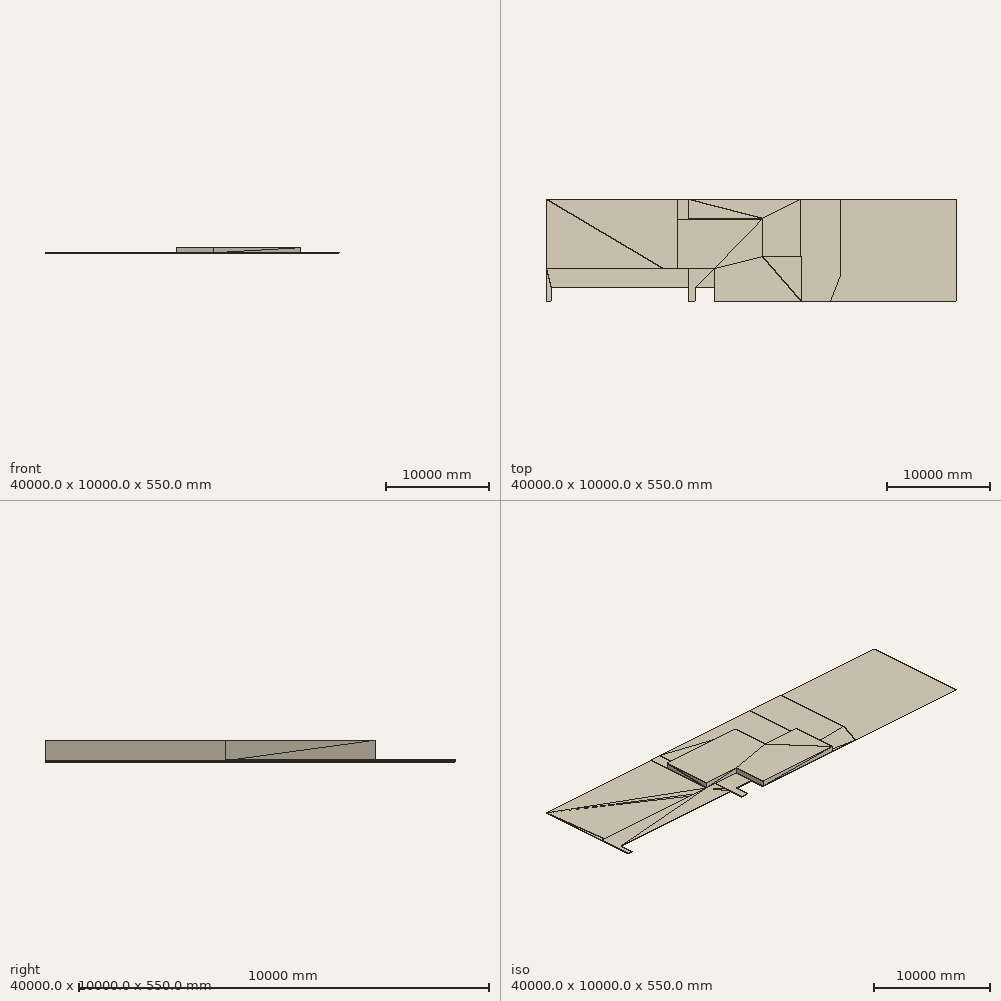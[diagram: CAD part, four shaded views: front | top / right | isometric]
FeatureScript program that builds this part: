
annotation { "Feature Type Name" : "Feature", "Feature Type Description" : "" }
export const myFeature = defineFeature(function(context is Context, id is Id, definition is map)
    precondition{}
    {
        {
            var Q0;
            Q0=qCreatedBy(makeId("Top.planeOp"),FACE);
            var sketch = newSketch(context, id + "F0", { "sketchPlane" : qUnion([Q0])});
            skLineSegment(sketch, "E0.bottom", {"start": v(-20000, -5000) * mm, "end": v(20000, -5000) * mm});
            skLineSegment(sketch, "E0.top", {"start": v(-20000, 5000) * mm, "end": v(20000, 5000) * mm});
            skLineSegment(sketch, "E0.left", {"start": v(-20000, -5000) * mm, "end": v(-20000, 5000) * mm});
            skLineSegment(sketch, "E0.right", {"start": v(20000, -5000) * mm, "end": v(20000, 5000) * mm});
            skPoint(sketch, "E0.middle", {"position": v(0, 0) * mm});
            skSolve(sketch);
        }
        {
            var Q0;
            Q0 = qSketchRegion(id + "F0", true);
            extrude(context, id + "F1", {"entities" : qUnion([Q0]), "depth" : 25 * mm});
        }
        {
            var Q0;
            Q0=makeQuery(id+"F1.opExtrude","CAP_FACE",FACE,{"disambiguationData":[OSD([sQuery(id+"F0.wireOp",EDGE,"E0.bottom"),sQuery(id+"F0.wireOp",EDGE,"E0.top"),sQuery(id+"F0.wireOp",EDGE,"E0.left"),sQuery(id+"F0.wireOp",EDGE,"E0.right")])],"isStart":false});
            var sketch = newSketch(context, id + "F2", { "sketchPlane" : qUnion([Q0])});
            skLineSegment(sketch, "E1", {"start": v(-20000, -5000) * mm, "end": v(-20000, -1769.44) * mm});
            skLineSegment(sketch, "E2", {"start": v(-20000, -1769.44) * mm, "end": v(-7233.33, -1769.44) * mm});
            skLineSegment(sketch, "E3", {"start": v(-7233.33, -1769.44) * mm, "end": v(-7233.33, 5000) * mm});
            skLineSegment(sketch, "E4", {"start": v(-7233.33, 5000) * mm, "end": v(8633.33, 5000) * mm});
            skLineSegment(sketch, "E5", {"start": v(8633.33, 5000) * mm, "end": v(8633.33, -2625) * mm});
            skLineSegment(sketch, "E6", {"start": v(8633.33, -2625) * mm, "end": v(7700, -5000) * mm});
            skLineSegment(sketch, "E7", {"start": v(7700, -5000) * mm, "end": v(-20000, -5000) * mm});
            skSolve(sketch);
        }
        {
            var Q0;
            Q0 = qSketchRegion(id + "F2", true);
            extrude(context, id + "F3", {"entities" : qUnion([Q0]), "depth" : 25 * mm});
        }
        {
            var Q0;
            Q0=makeQuery(id+"F3.opExtrude","CAP_FACE",FACE,{"disambiguationData":[OSD([sQuery(id+"F2.wireOp",EDGE,"E1"),sQuery(id+"F2.wireOp",EDGE,"E2"),sQuery(id+"F2.wireOp",EDGE,"E3"),sQuery(id+"F2.wireOp",EDGE,"E4"),sQuery(id+"F2.wireOp",EDGE,"E5"),sQuery(id+"F2.wireOp",EDGE,"E6"),sQuery(id+"F2.wireOp",EDGE,"E7")])],"isStart":false});
            var sketch = newSketch(context, id + "F4", { "sketchPlane" : qUnion([Q0])});
            skLineSegment(sketch, "E8", {"start": v(-6150, -5000) * mm, "end": v(-6150, -1769.44) * mm});
            skLineSegment(sketch, "E9", {"start": v(-6150, -1769.44) * mm, "end": v(-3583.33, -1769.44) * mm});
            skLineSegment(sketch, "E10", {"start": v(-3583.33, -1769.44) * mm, "end": v(-3583.33, -5000) * mm});
            skLineSegment(sketch, "E11", {"start": v(-6150, 5000) * mm, "end": v(-6150, 3130.56) * mm});
            skLineSegment(sketch, "E12", {"start": v(-6150, 3130.56) * mm, "end": v(1083.33, 3130.56) * mm});
            skLineSegment(sketch, "E13", {"start": v(1083.33, 3130.56) * mm, "end": v(1083.33, -602.78) * mm});
            skLineSegment(sketch, "E14", {"start": v(1083.33, -602.78) * mm, "end": v(4816.67, -602.78) * mm});
            skLineSegment(sketch, "E15", {"start": v(4816.67, -602.78) * mm, "end": v(4816.67, 5000) * mm});
            skLineSegment(sketch, "E16", {"start": v(4816.67, 5000) * mm, "end": v(-6150, 5000) * mm});
            skSolve(sketch);
        }
        {
            var Q0;
            {var subQ0=sQuery(id+"F4.wireOp",EDGE,"E8");Q0=makeQuery(id+"F4.imprint","IMPRINT",FACE,{"disambiguationData":[TD([[makeQuery(id+"F4.imprint","IMPRINT",EDGE,{"derivedFrom":subQ0}),-1.0]])]});}
            var Q1;
            Q1=makeQuery(id+"F4.imprint","IMPRINT",FACE,{"disambiguationData":[TD([[makeQuery(id+"F4.imprint","IMPRINT",EDGE,{"derivedFrom":sQuery(id+"F4.wireOp",EDGE,"E11")}),1.0]])]});
            extrude(context, id + "F5", {"entities" : qUnion([Q0, Q1]), "depth" : 25 * mm});
        }
        {
            var Q0;
            Q0=makeQuery(id+"F3.opExtrude","CAP_FACE",FACE,{"disambiguationData":[OSD([sQuery(id+"F2.wireOp",EDGE,"E1"),sQuery(id+"F2.wireOp",EDGE,"E2"),sQuery(id+"F2.wireOp",EDGE,"E3"),sQuery(id+"F2.wireOp",EDGE,"E4"),sQuery(id+"F2.wireOp",EDGE,"E5"),sQuery(id+"F2.wireOp",EDGE,"E6"),sQuery(id+"F2.wireOp",EDGE,"E7")])],"isStart":false});
            var sketch = newSketch(context, id + "F6", { "sketchPlane" : qUnion([Q0])});
            skLineSegment(sketch, "E17", {"start": v(-7233.33, -1769.44) * mm, "end": v(-3583.33, -1769.44) * mm});
            skLineSegment(sketch, "E18", {"start": v(-3583.33, -1769.44) * mm, "end": v(-3583.33, -5000) * mm});
            skLineSegment(sketch, "E19", {"start": v(-3583.33, -5000) * mm, "end": v(4894.44, -5000) * mm});
            skLineSegment(sketch, "E20", {"start": v(4894.44, -5000) * mm, "end": v(4894.44, -602.78) * mm});
            skLineSegment(sketch, "E21", {"start": v(4894.44, -602.78) * mm, "end": v(1083.33, -602.78) * mm});
            skLineSegment(sketch, "E22", {"start": v(1083.33, -602.78) * mm, "end": v(1083.33, 3052.78) * mm});
            skLineSegment(sketch, "E23", {"start": v(1083.33, 3052.78) * mm, "end": v(-7233.33, 3052.78) * mm});
            skLineSegment(sketch, "E24", {"start": v(-7233.33, 3052.78) * mm, "end": v(-7233.33, -1769.44) * mm});
            skSolve(sketch);
        }
        {
            var Q0;
            Q0 = qSketchRegion(id + "F6", true);
            extrude(context, id + "F7", {"entities" : qUnion([Q0]), "depth" : 500 * mm});
        }
        {
            var Q0;
            Q0=makeQuery(id+"F3.opExtrude","CAP_FACE",FACE,{"disambiguationData":[OSD([sQuery(id+"F2.wireOp",EDGE,"E1"),sQuery(id+"F2.wireOp",EDGE,"E2"),sQuery(id+"F2.wireOp",EDGE,"E3"),sQuery(id+"F2.wireOp",EDGE,"E4"),sQuery(id+"F2.wireOp",EDGE,"E5"),sQuery(id+"F2.wireOp",EDGE,"E6"),sQuery(id+"F2.wireOp",EDGE,"E7")])],"isStart":false});
            var sketch = newSketch(context, id + "F8", { "sketchPlane" : qUnion([Q0])});
            skLineSegment(sketch, "E25.bottom", {"start": v(-19527.78, -5000) * mm, "end": v(-6150, -5000) * mm});
            skLineSegment(sketch, "E25.top", {"start": v(-19527.78, -3636.11) * mm, "end": v(-6150, -3636.11) * mm});
            skLineSegment(sketch, "E25.left", {"start": v(-19527.78, -5000) * mm, "end": v(-19527.78, -3636.11) * mm});
            skLineSegment(sketch, "E25.right", {"start": v(-6150, -5000) * mm, "end": v(-6150, -3636.11) * mm});
            skLineSegment(sketch, "E26.bottom", {"start": v(-5450, -5000) * mm, "end": v(-3583.33, -5000) * mm});
            skLineSegment(sketch, "E26.top", {"start": v(-5450, -3636.11) * mm, "end": v(-3583.33, -3636.11) * mm});
            skLineSegment(sketch, "E26.left", {"start": v(-5450, -5000) * mm, "end": v(-5450, -3636.11) * mm});
            skLineSegment(sketch, "E26.right", {"start": v(-3583.33, -5000) * mm, "end": v(-3583.33, -3636.11) * mm});
            skSolve(sketch);
        }
        {
            var Q0;
            Q0 = qSketchRegion(id + "F8", true);
            extrude(context, id + "F9", {"entities" : qUnion([Q0]), "operationType" : NewBodyOperationType.REMOVE, "endBound" : BoundingType.SYMMETRIC, "oppositeDirection" : true, "depth" : 4200 * mm});
        }
    });
